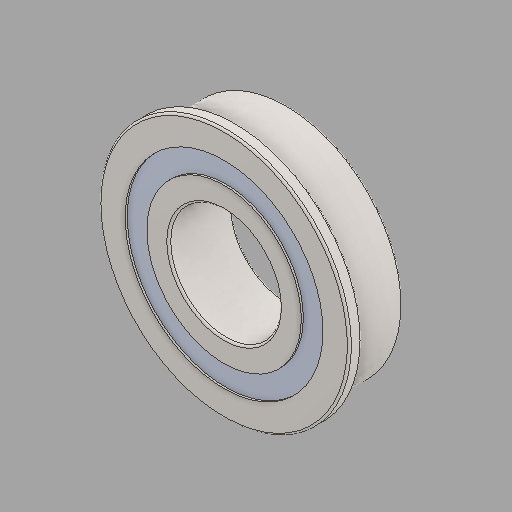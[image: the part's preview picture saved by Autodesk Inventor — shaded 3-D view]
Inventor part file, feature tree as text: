
AUTODESK INVENTOR PART (.ipt)
format: ipt  version: 2024.2 (Build 282272000, 272)  size: 190,464 bytes
history: native  units: in
note: dims shown in document units (in); Inventor stores cm internally (conversion verified against a paired STEP export)
features: fillet x1
ambient origin geometry x8: Origin, YZ Plane, XZ Plane, XY Plane, X Axis, Y Axis, Z Axis, Center Point
bodies: Solid1 (feature_tree)
feature tree (1):
  fillet  "Fillet1"  [1 undecoded]
note: 1 required parameter value undecoded (feature->parameter linkage not recoverable at this tier; creation-order binding heuristic only, values carry confidence <= 0.55)
